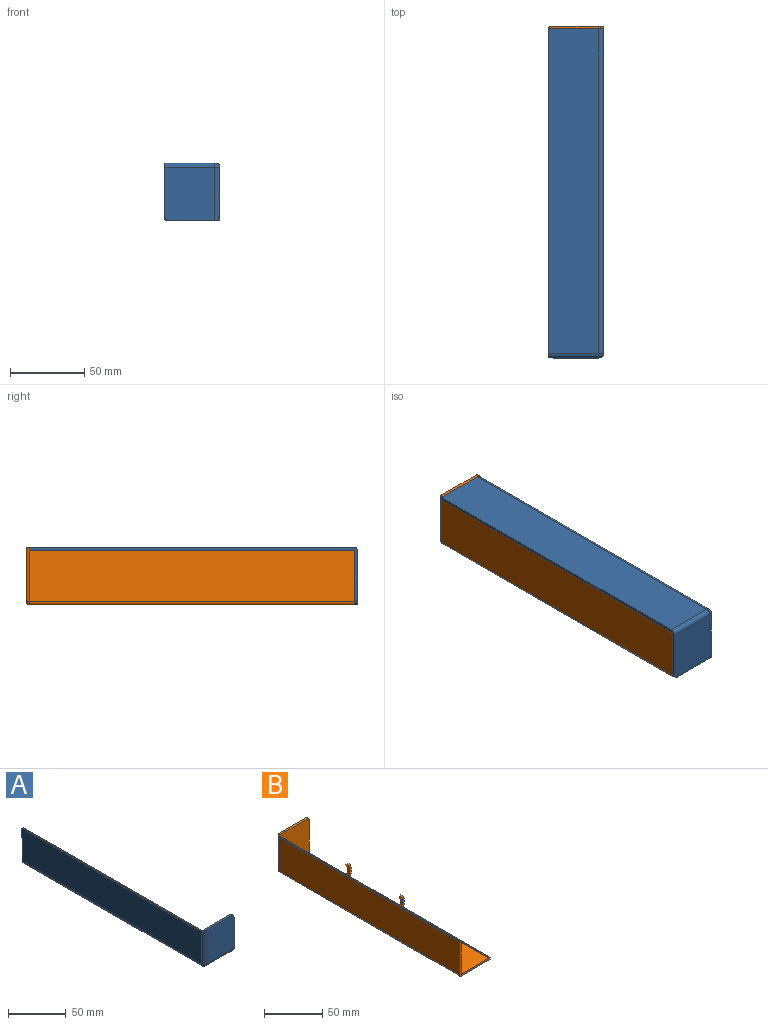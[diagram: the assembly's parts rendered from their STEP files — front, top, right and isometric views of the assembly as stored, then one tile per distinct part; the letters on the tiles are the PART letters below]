
ASSEMBLY  parts=2 mates=1
PART A: 37 faces, bbox 37x222x39 mm
  f0: cylinder r=3.5mm len=3.18mm, axis (0,-1,0), area 8mm2, adj f1,f2,f28,f35
  f1: plane 5.99x4.06mm, normal (0,-1,0), area 14.4mm2, adj f0,f11,f26,f27,f28,f35
  f2: plane 5.99x4.06mm, normal (0,1,0), area 14.4mm2, adj f0,f11,f26,f27,f28,f35
  f3: plane 220x0.7mm, normal (0,0,1), area 154mm2, adj f5,f7,f16,f18
  f4: plane 220x0.68mm, normal (0,0,1), area 148.4mm2, adj f5,f6,f13,f18,f22
  f5: plane 37x37mm, normal (0,1,0), area 142mm2, adj f3,f4,f6,f7,f8,f9,f10,f11
  f6: plane 219x34mm, normal (-1,0,0), area 7446mm2, adj f4,f5,f21,f22
  f7: plane 222x36mm, normal (1,0,0), area 510.1mm2, adj f3,f5,f9,f18,f20,f24,f25
  f8: plane 220x33.7mm, normal (0,0,1), area 7414mm2, adj f5,f11,f15,f18
  f9: plane 219x34mm, normal (0,0,-1), area 7446mm2, adj f5,f7,f21,f24
  f10: plane 220x0.68mm, normal (0,0,1), area 148.5mm2, adj f5,f11,f12,f18
  f11: plane 220x35mm, normal (1,0,0), area 7690mm2, adj f1,f2,f5,f8,f10,f18,f26,f32
  f12: plane 220x0.77mm, normal (-0.97,0,-0.25), area 176mm2, adj f5,f10,f14,f18
  f13: plane 220x0.77mm, normal (0.97,0,-0.25), area 176mm2, adj f4,f5,f14,f18
  f14: plane 220x1.05mm, normal (0,0,1), area 231mm2, adj f5,f12,f13,f18
  f15: plane 220x0.77mm, normal (-0.97,0,-0.25), area 176mm2, adj f5,f8,f17,f18
  f16: plane 220x0.77mm, normal (0.97,0,-0.25), area 176mm2, adj f3,f5,f17,f18
  f17: plane 220x1mm, normal (0,0,1), area 220mm2, adj f5,f15,f16,f18
  f18: plane 37x36.83mm, normal (0,1,0), area 1296.8mm2, adj f3,f4,f7,f8,f10,f11,f12,f13
  f19: plane 33.83x2mm, normal (0,0,1), area 66.1mm2, adj f18,f20,f22,f25
  f20: plane 36x34mm, normal (0,-1,0), area 1222.1mm2, adj f7,f19,f22,f24,f25
  f21: cylinder r=3mm len=219mm, axis (0,-1,0), area 1032mm2, adj f5,f6,f9,f23
  f22: cylinder r=3mm len=36mm, axis (0,0,-1), area 167.6mm2, adj f4,f6,f18,f19,f20,f23
  f23: sphere r=3mm, area 14.1mm2, adj f21,f22,f24
  f24: cylinder r=3mm len=34mm, axis (-1,0,0), area 160.2mm2, adj f7,f9,f20,f23
  f25: cylinder r=3mm len=3mm, axis (0,1,0), area 9.4mm2, adj f7,f18,f19,f20
  f26: plane 2.16x2mm, normal (0,0,-1), area 4.3mm2, adj f1,f2,f11,f27
  f27: cylinder r=5.5mm len=3.83mm, axis (0,-1,0), area 8.5mm2, adj f1,f2,f26,f28
  f28: plane 2x2mm, normal (1,0,0), area 4mm2, adj f0,f1,f2,f27
  f29: cylinder r=3.5mm len=3.51mm, axis (0,-1,0), area 9.9mm2, adj f30,f33,f34,f36
  f30: plane 2x2mm, normal (1,0,0), area 4mm2, adj f29,f31,f33,f34
  f31: cylinder r=5.5mm len=4.6mm, axis (0,-1,0), area 10.8mm2, adj f30,f32,f33,f34
  f32: plane 2x1.47mm, normal (0,0,1), area 2.9mm2, adj f11,f31,f33,f34
  f33: plane 6.07x4.88mm, normal (0,-1,0), area 15.2mm2, adj f11,f29,f30,f31,f32,f36
  f34: plane 6.07x4.88mm, normal (0,1,0), area 15.2mm2, adj f11,f29,f30,f31,f32,f36
  f35: plane 2.81x2mm, normal (0,0,1), area 5.6mm2, adj f0,f1,f2,f11
  f36: plane 2.56x2mm, normal (0,0,-1), area 5.1mm2, adj f11,f29,f33,f34
PART B: 51 faces, bbox 37x222x39 mm
  f0: plane 220x0.7mm, normal (0,0,1), area 154mm2, adj f3,f4,f13,f17
  f1: plane 220x0.68mm, normal (0,0,1), area 148.5mm2, adj f2,f3,f10,f17
  f2: plane 220x35mm, normal (-1,0,0), area 7700mm2, adj f1,f3,f18,f19
  f3: plane 37x37mm, normal (0,-1,0), area 143.1mm2, adj f0,f1,f2,f4,f5,f6,f7,f8
  f4: plane 222x37mm, normal (1,0,0), area 513.1mm2, adj f0,f3,f6,f16,f17,f21,f22
  f5: plane 220x33.7mm, normal (0,0,1), area 7360mm2, adj f3,f8,f12,f17,f23,f27,f28,f29
  f6: plane 220x35mm, normal (0,0,-1), area 7700mm2, adj f3,f4,f19,f21
  f7: plane 220x0.68mm, normal (0,0,1), area 148.5mm2, adj f3,f8,f9,f17
  f8: plane 220x35mm, normal (1,0,0), area 7700mm2, adj f3,f5,f7,f17
  f9: plane 220x0.77mm, normal (-0.97,0,-0.25), area 176mm2, adj f3,f7,f11,f17
  f10: plane 220x0.77mm, normal (0.97,0,-0.25), area 176mm2, adj f1,f3,f11,f17
  f11: plane 220x1.05mm, normal (0,0,1), area 231mm2, adj f3,f9,f10,f17
  f12: plane 220x0.77mm, normal (-0.97,0,-0.25), area 176mm2, adj f3,f5,f14,f17
  f13: plane 220x0.77mm, normal (0.97,0,-0.25), area 176mm2, adj f0,f3,f14,f17
  f14: plane 220x1mm, normal (0,0,1), area 220mm2, adj f3,f12,f13,f17
  f15: plane 35x2mm, normal (0,0,1), area 69.1mm2, adj f16,f17,f18,f22
  f16: plane 37x35mm, normal (0,1,0), area 1294.1mm2, adj f4,f15,f18,f21,f22
  f17: plane 37x37mm, normal (0,-1,0), area 1298.2mm2, adj f0,f1,f4,f5,f7,f8,f9,f10
  f18: cylinder r=2mm len=37mm, axis (0,0,-1), area 116.2mm2, adj f2,f15,f16,f17,f20
  f19: cylinder r=2mm len=220mm, axis (0,-1,0), area 691.2mm2, adj f2,f3,f6,f20
  f20: sphere r=2mm, area 6.3mm2, adj f18,f19,f21
  f21: cylinder r=2mm len=35mm, axis (1,0,0), area 110mm2, adj f4,f6,f16,f20
  f22: cylinder r=2mm len=2mm, axis (0,1,0), area 6.3mm2, adj f4,f15,f16,f17
  f23: plane 3x2mm, normal (1,0,0), area 6mm2, adj f5,f24,f28,f29
  f24: cylinder r=14mm len=18.87mm, axis (0,-1,0), area 66.7mm2, adj f23,f25,f28,f29
  f25: plane 3x2.28mm, normal (0,0,1), area 6.8mm2, adj f24,f26,f28,f29
  f26: cylinder r=12mm len=18.12mm, axis (0,-1,0), area 71.6mm2, adj f25,f27,f28,f29
  f27: plane 3x2.74mm, normal (-1,0,0), area 8.2mm2, adj f5,f26,f28,f29
  f28: plane 20.87x12.5mm, normal (0,-1,0), area 56.3mm2, adj f5,f23,f24,f25,f26,f27
  f29: plane 20.87x12.5mm, normal (0,1,0), area 56.3mm2, adj f5,f23,f24,f25,f26,f27
  f30: plane 3x2.33mm, normal (0,0,1), area 7mm2, adj f31,f34,f35,f36
  f31: cylinder r=14mm len=19.29mm, axis (0,-1,0), area 68.1mm2, adj f30,f32,f35,f36
  f32: plane 3x2mm, normal (-1,0,0), area 6mm2, adj f5,f31,f35,f36
  f33: plane 3x2.74mm, normal (1,0,0), area 8.2mm2, adj f5,f34,f35,f36
  f34: cylinder r=12mm len=18.54mm, axis (0,-1,0), area 73.1mm2, adj f30,f33,f35,f36
  f35: plane 21.29x12.5mm, normal (0,-1,0), area 57.3mm2, adj f5,f30,f31,f32,f33,f34
  f36: plane 21.29x12.5mm, normal (0,1,0), area 57.3mm2, adj f5,f30,f31,f32,f33,f34
  f37: plane 3x2mm, normal (1,0,0), area 6mm2, adj f5,f38,f42,f43
  f38: cylinder r=13.5mm len=18.24mm, axis (0,-1,0), area 64.1mm2, adj f37,f39,f42,f43
  f39: plane 3x2.09mm, normal (-0.16,0,0.99), area 6.4mm2, adj f38,f40,f42,f43
  f40: cylinder r=11.5mm len=17.22mm, axis (0,-1,0), area 68.2mm2, adj f39,f41,f42,f43
  f41: plane 3x2.68mm, normal (-1,0,0), area 8mm2, adj f5,f40,f42,f43
  f42: plane 20.24x12.09mm, normal (0,-1,0), area 54.4mm2, adj f5,f37,f38,f39,f40,f41
  f43: plane 20.24x12.09mm, normal (0,1,0), area 54.4mm2, adj f5,f37,f38,f39,f40,f41
  f44: cylinder r=11.5mm len=17.53mm, axis (0,-1,0), area 68.8mm2, adj f45,f48,f49,f50
  f45: plane 3x2.3mm, normal (0,0,1), area 6.9mm2, adj f44,f46,f49,f50
  f46: cylinder r=13.5mm len=18.24mm, axis (0,-1,0), area 64.1mm2, adj f45,f47,f49,f50
  f47: plane 3x2mm, normal (-1,0,0), area 6mm2, adj f5,f46,f49,f50
  f48: plane 3x2.7mm, normal (1,0,0), area 8.1mm2, adj f5,f44,f49,f50
  f49: plane 20.24x11.91mm, normal (0,-1,0), area 54.2mm2, adj f5,f44,f45,f46,f47,f48
  f50: plane 20.24x11.91mm, normal (0,1,0), area 54.2mm2, adj f5,f44,f45,f46,f47,f48
PLACE A rot(axis=(0,-1,0),180deg) t=(-79.36,57.83,-0.53)mm
PLACE B rot(axis=(-1,0,0),0deg) t=(-116.39,57.83,-39.53)mm
MATE fastened B.f3 <-> A.f18  axis (0,-1,0) through (-114.86,-162.17,-3.3)mm
